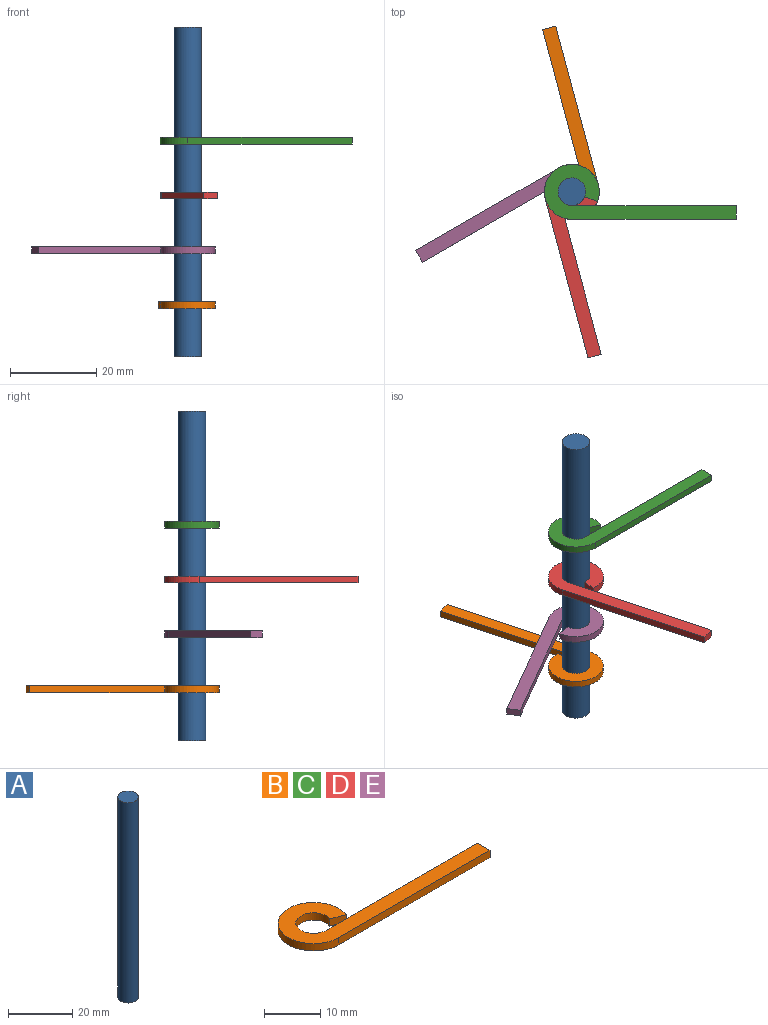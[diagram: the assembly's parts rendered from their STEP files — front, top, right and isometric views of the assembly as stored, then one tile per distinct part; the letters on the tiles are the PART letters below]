
ASSEMBLY  parts=5 mates=4
PART A: 3 faces, bbox 6.4x6.4x76.2 mm
  f0: cylinder r=3.17mm len=76.2mm, axis (0,0,-1), area 1520.1mm2, adj f1,f2
  f1: plane 6.35x6.35mm, normal (0,0,1), area 31.7mm2, adj f0
  f2: plane 6.35x6.35mm, normal (0,0,-1), area 31.7mm2, adj f0
PART B: 8 faces, bbox 44.5x12.7x1.6 mm
  f0: cylinder r=6.35mm len=12.7mm, axis (0,0,-1), area 51.2mm2, adj f1,f5,f6,f7
  f1: plane 38.1x1.59mm, normal (0,-1,0), area 60.5mm2, adj f0,f2,f6,f7
  f2: plane 3.18x1.59mm, normal (1,0,0), area 5mm2, adj f1,f3,f6,f7
  f3: plane 38.1x1.59mm, normal (0,1,0), area 60.5mm2, adj f2,f4,f6,f7
  f4: cylinder r=3.17mm len=6.35mm, axis (0,0,-1), area 25.6mm2, adj f3,f5,f6,f7
  f5: plane 2.97x1.59mm, normal (-0.36,-0.93,0), area 5mm2, adj f0,f4,f6,f7
  f6: plane 44.45x12.7mm, normal (0,0,1), area 197.7mm2, adj f0,f1,f2,f3,f4,f5
  f7: plane 44.45x12.7mm, normal (0,0,-1), area 197.7mm2, adj f0,f1,f2,f3,f4,f5
PART C: same geometry as B
PART D: same geometry as B
PART E: same geometry as B
PLACE A rot(axis=(0,0,1),105deg) t=(-48.93,13.8,39.55)mm
PLACE B rot(axis=(0,0,1),105deg) t=(-71.35,111.78,50.66)mm
PLACE C t=(-25.09,-10.12,88.76)mm
PLACE D rot(axis=(0,0,-1),75deg) t=(-118.62,-45.62,76.06)mm
PLACE E rot(axis=(0,0,-1),150deg) t=(-177.12,35.54,63.36)mm
MATE revolute A.f0 <-> C.f0  axis (0,0,1) through (-94.98,33.08,115.75)mm
MATE revolute E.f0 <-> A.f0  axis (0,0,1) through (-94.98,33.08,64.95)mm
MATE revolute A.f0 <-> D.f0  axis (0,0,1) through (-94.98,33.08,115.75)mm
MATE revolute A.f0 <-> B.f0  axis (0,0,-1) through (-94.98,33.08,115.75)mm
